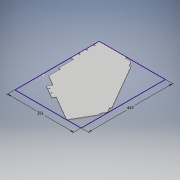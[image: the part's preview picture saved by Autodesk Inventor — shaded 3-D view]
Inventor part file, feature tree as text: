
AUTODESK INVENTOR PART (.ipt)
format: ipt  version: 2019.4 (Build 234330000, 330)  size: 221,184 bytes
history: native  units: mm
features: sketch x7, extrude x5, fillet x1
ambient origin geometry x8: Origin, YZ Plane, XZ Plane, XY Plane, X Axis, Y Axis, Z Axis, Center Point
bodies: Solid1 (feature_tree)
feature tree (13):
  extrude  "Extrusion1"  Depth=303.0mm
  extrude  "Extrusion2"  Depth=16.0mm
  extrude  "Extrusion3"  Depth=30.0mm TaperAngle=360.0deg
  extrude  "Extrusion4"  Depth=151.5mm
  extrude  "Extrusion5"  Depth=152.5mm
  sketch  "Sketch6"  dims[d15=3.0mm d16=0.0mm]
  sketch  "Sketch7"  dims[d17=35.0mm d18=8.0mm d19=35.0mm d20=8.0mm d21=35.0mm d22=8.0mm d23=35.0mm d24=120.0deg d25=8.0mm d26=3.0mm d27=0.0mm d28=145.0mm d29=30.0deg d30=35.0mm d31=145.0mm d32=90.0deg d33=35.0mm d34=3.0mm d35=0.0mm d36=40.0mm d37=5.5mm d38=30.0mm d40=40.0mm d41=10.0mm d43=10.0mm d45=1.0mm d46=6.5mm d47=30.0mm d48=30.0mm d49=5.5mm d50=5.5mm d51=3.0mm d52=0.0mm d53=7.0mm d54=352.0mm d55=450.0mm d56=351.0mm d57=447.0mm d58=10.0mm]
  fillet  "Fillet1"  Radius=17.0mm
  sketch  "Sketch1"  dims[d0=303.0mm d1=303.0mm]
  sketch  "Sketch2"  dims[d2=8.0mm d3=16.0mm]
  sketch  "Sketch3"  dims[d4=5.0mm d5=30.0mm d7=360.0deg]
  sketch  "Sketch4"  dims[d9=3.0mm d10=0.0mm d11=151.5mm]
  sketch  "Sketch5"  dims[d12=16.0mm d13=152.5mm d14=17.0mm]
